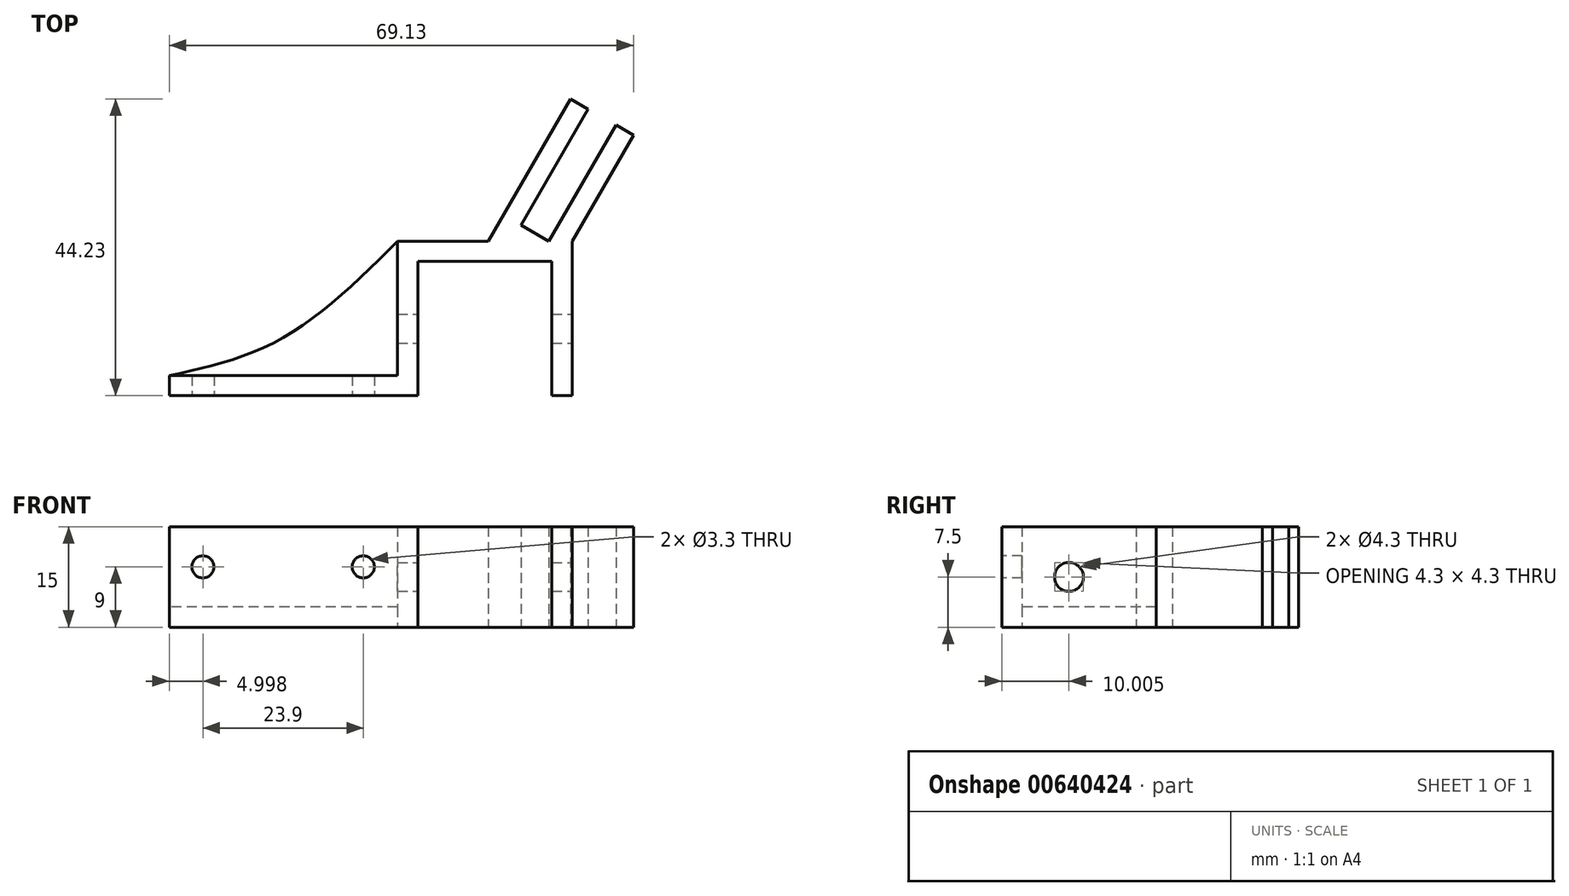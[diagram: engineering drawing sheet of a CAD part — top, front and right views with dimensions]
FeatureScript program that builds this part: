
annotation { "Feature Type Name" : "Feature", "Feature Type Description" : "" }
export const myFeature = defineFeature(function(context is Context, id is Id, definition is map)
    precondition{}
    {
        {
            var Q0;
            Q0=qCreatedBy(makeId("Top.planeOp"),FACE);
            var sketch = newSketch(context, id + "F0", { "sketchPlane" : qUnion([Q0])});
            skLineSegment(sketch, "E0", {"start": v(-53.41, 6.85) * mm, "end": v(-16.41, 6.85) * mm});
            skLineSegment(sketch, "E1", {"start": v(-16.41, 6.85) * mm, "end": v(-16.41, 26.85) * mm});
            skLineSegment(sketch, "E2", {"start": v(-16.41, 26.85) * mm, "end": v(3.59, 26.85) * mm});
            skLineSegment(sketch, "E3", {"start": v(3.59, 26.85) * mm, "end": v(3.59, 6.85) * mm});
            skLineSegment(sketch, "E4", {"start": v(3.59, 6.85) * mm, "end": v(6.59, 6.85) * mm});
            skLineSegment(sketch, "E5", {"start": v(6.59, 6.85) * mm, "end": v(6.59, 29.85) * mm});
            skLineSegment(sketch, "E6", {"start": v(-19.41, 29.85) * mm, "end": v(-19.41, 9.85) * mm});
            skLineSegment(sketch, "E7", {"start": v(-19.41, 9.85) * mm, "end": v(-53.41, 9.85) * mm});
            skLineSegment(sketch, "E8", {"start": v(-53.41, 9.85) * mm, "end": v(-53.41, 6.85) * mm});
            skLineSegment(sketch, "E9", {"start": v(6.59, 29.85) * mm, "end": v(15.72, 45.68) * mm});
            skLineSegment(sketch, "E10", {"start": v(3.12, 29.85) * mm, "end": v(13.12, 47.18) * mm});
            skLineSegment(sketch, "E11", {"start": v(-1.03, 32.25) * mm, "end": v(8.97, 49.58) * mm});
            skLineSegment(sketch, "E12", {"start": v(-5.88, 29.85) * mm, "end": v(6.37, 51.08) * mm});
            skLineSegment(sketch, "E13", {"start": v(13.12, 47.18) * mm, "end": v(15.72, 45.68) * mm});
            skLineSegment(sketch, "E14", {"start": v(8.97, 49.58) * mm, "end": v(6.37, 51.08) * mm});
            skLineSegment(sketch, "E15.trimOffspring", {"start": v(-5.88, 29.85) * mm, "end": v(-19.41, 29.85) * mm});
            skLineSegment(sketch, "E16", {"start": v(3.12, 29.85) * mm, "end": v(-1.03, 32.25) * mm});
            skFitSpline(sketch, "E17", {"points": [v(-19.41, 29.85) * mm, v(-36.8, 15.3) * mm, v(-53.41, 9.85) * mm], "startDerivative": vector(-31.88, -31.5) * mm, "endDerivative": vector(-36.2, -8) * mm});
            skSolve(sketch);
        }
        {
            var Q0;
            Q0=makeQuery(id+"F0.imprint","IMPRINT",FACE,{"disambiguationData":[TD([[makeQuery(id+"F0.imprint","IMPRINT",EDGE,{"derivedFrom":sQuery(id+"F0.wireOp",EDGE,"E0")}),1.0]])]});
            extrude(context, id + "F1", {"entities" : qUnion([Q0]), "depth" : 15 * mm, "offsetDistance" : 25 * mm});
        }
        {
            var Q0;
            Q0=makeQuery(id+"F0.imprint","IMPRINT",FACE,{"disambiguationData":[TD([[makeQuery(id+"F0.imprint","IMPRINT",EDGE,{"derivedFrom":sQuery(id+"F0.wireOp",EDGE,"E6")}),-1.0]])]});
            extrude(context, id + "F2", {"entities" : qUnion([Q0]), "operationType" : NewBodyOperationType.ADD, "depth" : 3 * mm, "offsetDistance" : 25 * mm});
        }
        {
            var Q0;
            Q0=makeQuery(id+"F1.opExtrude","SWEPT_FACE",FACE,{"disambiguationData":[OSD([sQuery(id+"F0.wireOp",EDGE,"E0")])]});
            var sketch = newSketch(context, id + "F3", { "sketchPlane" : qUnion([Q0])});
            skLineSegment(sketch, "E18", {"start": v(-65.46, 9) * mm, "end": v(-2.65, 9) * mm, "construction": true});
            skLineSegment(sketch, "E19", {"start": v(-24.51, 19.55) * mm, "end": v(-24.51, -3.98) * mm, "construction": true});
            skLineSegment(sketch, "E20", {"start": v(-48.41, 19.92) * mm, "end": v(-48.41, -2.55) * mm, "construction": true});
            skCircle(sketch, "E21", {"center": v(-48.41, 9) * mm, "radius": 1.65 * mm});
            skCircle(sketch, "E22", {"center": v(-24.51, 9) * mm, "radius": 1.65 * mm});
            skSolve(sketch);
        }
        {
            var Q0;
            Q0=makeQuery(id+"F3.imprint","IMPRINT",FACE,{"disambiguationData":[TD([[makeQuery(id+"F3.imprint","IMPRINT",EDGE,{"derivedFrom":sQuery(id+"F3.wireOp",EDGE,"E21")}),1.0]])]});
            var Q1;
            Q1=makeQuery(id+"F3.imprint","IMPRINT",FACE,{"disambiguationData":[TD([[makeQuery(id+"F3.imprint","IMPRINT",EDGE,{"derivedFrom":sQuery(id+"F3.wireOp",EDGE,"E22")}),1.0]])]});
            extrude(context, id + "F4", {"entities" : qUnion([Q0, Q1]), "operationType" : NewBodyOperationType.REMOVE, "oppositeDirection" : true, "depth" : 5 * mm, "offsetDistance" : 25 * mm});
        }
        {
            var Q0;
            Q0=makeQuery(id+"F1.opExtrude","SWEPT_FACE",FACE,{"disambiguationData":[OSD([sQuery(id+"F0.wireOp",EDGE,"E5")])]});
            var sketch = newSketch(context, id + "F5", { "sketchPlane" : qUnion([Q0])});
            skCircle(sketch, "E23", {"center": v(16.85, 7.5) * mm, "radius": 2.15 * mm});
            skPoint(sketch, "E23.centerSnap0", {"position": v(6.85, 7.5) * mm});
            skSolve(sketch);
        }
        {
            var Q0;
            Q0=makeQuery(id+"F5.imprint","IMPRINT",FACE,{"disambiguationData":[TD([[makeQuery(id+"F5.imprint","IMPRINT",EDGE,{"derivedFrom":sQuery(id+"F5.wireOp",EDGE,"E23")}),1.0]])]});
            extrude(context, id + "F6", {"entities" : qUnion([Q0]), "operationType" : NewBodyOperationType.REMOVE, "oppositeDirection" : true, "depth" : 30 * mm, "offsetDistance" : 25 * mm});
        }
    });
